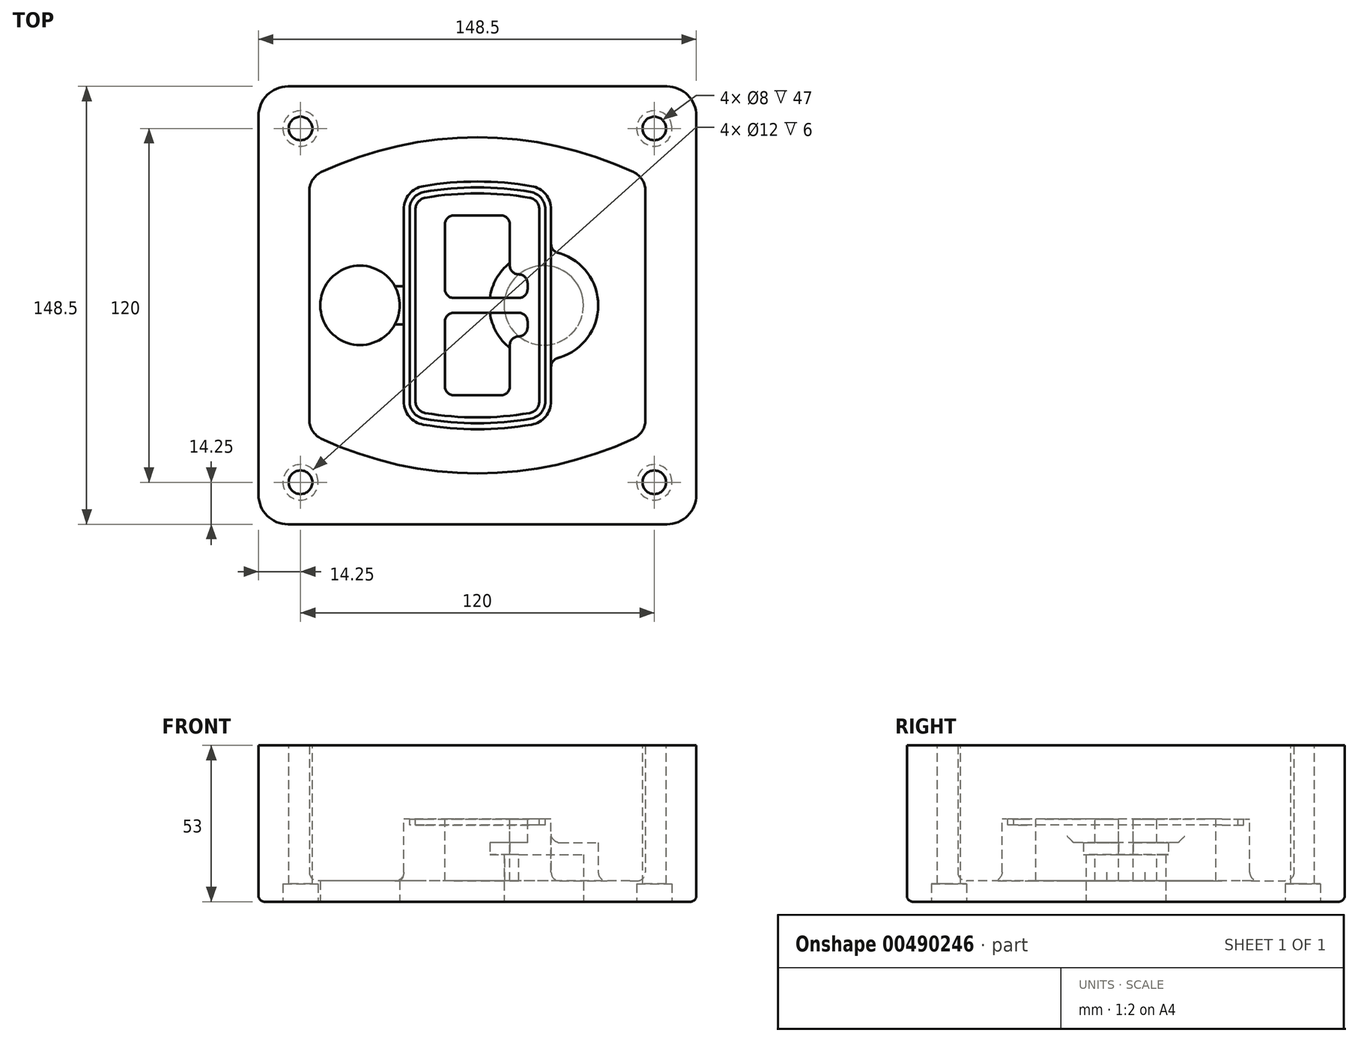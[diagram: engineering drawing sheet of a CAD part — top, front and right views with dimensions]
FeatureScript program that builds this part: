
annotation { "Feature Type Name" : "Feature", "Feature Type Description" : "" }
export const myFeature = defineFeature(function(context is Context, id is Id, definition is map)
    precondition{}
    {
        {
            var Q0;
            Q0=qCreatedBy(makeId("Top.planeOp"),FACE);
            var sketch = newSketch(context, id + "F0", { "sketchPlane" : qUnion([Q0])});
            skPoint(sketch, "E0.rect.middle", {"position": v(0, 0) * mm});
            skLineSegment(sketch, "E1.bottom", {"start": v(-64.25, -74.25) * mm, "end": v(64.25, -74.25) * mm});
            skLineSegment(sketch, "E1.top", {"start": v(-64.25, 74.25) * mm, "end": v(64.25, 74.25) * mm});
            skLineSegment(sketch, "E1.left", {"start": v(-74.25, -64.25) * mm, "end": v(-74.25, 64.25) * mm});
            skLineSegment(sketch, "E1.right", {"start": v(74.25, -64.25) * mm, "end": v(74.25, 64.25) * mm});
            skLineSegment(sketch, "E2", {"start": v(-74.25, 74.25) * mm, "end": v(74.25, -74.25) * mm, "construction": true});
            skLineSegment(sketch, "E3", {"start": v(74.25, 74.25) * mm, "end": v(-74.25, -74.25) * mm, "construction": true});
            skCircle(sketch, "E4", {"center": v(-60, 60) * mm, "radius": 4 * mm});
            skCircle(sketch, "E5", {"center": v(60, 60) * mm, "radius": 4 * mm});
            skCircle(sketch, "E6", {"center": v(60, -60) * mm, "radius": 4 * mm});
            skCircle(sketch, "E7", {"center": v(-60, -60) * mm, "radius": 4 * mm});
            skLineSegment(sketch, "E8", {"start": v(-60, 60) * mm, "end": v(60, 60) * mm, "construction": true});
            skLineSegment(sketch, "E9", {"start": v(60, 60) * mm, "end": v(60, -60) * mm, "construction": true});
            skLineSegment(sketch, "E10", {"start": v(60, -60) * mm, "end": v(-60, -60) * mm, "construction": true});
            skLineSegment(sketch, "E11", {"start": v(-60, -60) * mm, "end": v(-60, 60) * mm, "construction": true});
            skLineSegment(sketch, "E12", {"start": v(-60, 38.83) * mm, "end": v(-60, -38.83) * mm});
            skLineSegment(sketch, "E13", {"start": v(60, 38.83) * mm, "end": v(60, -38.83) * mm});
            skArc(sketch, "E14", {"start": v(54.26, 47.88) * mm, "mid": v(0, 60) * mm, "end": v(-54.26, 47.88) * mm});
            skArc(sketch, "E15", {"start": v(-54.26, -47.88) * mm, "mid": v(0, -60) * mm, "end": v(54.26, -47.88) * mm});
            skLineSegment(sketch, "E16", {"start": v(-60, 0) * mm, "end": v(60, 0) * mm, "construction": true});
            skPoint(sketch, "E17.visualSharp", {"position": v(-60, -45) * mm});
            skArc(sketch, "E17.filletArc", {"start": v(-60, -38.83) * mm, "mid": v(-58.44, -44.2) * mm, "end": v(-54.26, -47.88) * mm});
            skPoint(sketch, "E18.visualSharp", {"position": v(-60, 45) * mm});
            skArc(sketch, "E18.filletArc", {"start": v(-54.26, 47.88) * mm, "mid": v(-58.44, 44.2) * mm, "end": v(-60, 38.83) * mm});
            skPoint(sketch, "E19.visualSharp", {"position": v(60, 45) * mm});
            skArc(sketch, "E19.filletArc", {"start": v(60, 38.83) * mm, "mid": v(58.44, 44.2) * mm, "end": v(54.26, 47.88) * mm});
            skPoint(sketch, "E20.visualSharp", {"position": v(60, -45) * mm});
            skArc(sketch, "E20.filletArc", {"start": v(54.26, -47.88) * mm, "mid": v(58.44, -44.2) * mm, "end": v(60, -38.83) * mm});
            skPoint(sketch, "E21.visualSharp", {"position": v(-74.25, 74.25) * mm});
            skArc(sketch, "E21.filletArc", {"start": v(-64.25, 74.25) * mm, "mid": v(-71.32, 71.32) * mm, "end": v(-74.25, 64.25) * mm});
            skPoint(sketch, "E22.visualSharp", {"position": v(74.25, 74.25) * mm});
            skArc(sketch, "E22.filletArc", {"start": v(74.25, 64.25) * mm, "mid": v(71.32, 71.32) * mm, "end": v(64.25, 74.25) * mm});
            skPoint(sketch, "E23.visualSharp", {"position": v(74.25, -74.25) * mm});
            skArc(sketch, "E23.filletArc", {"start": v(64.25, -74.25) * mm, "mid": v(71.32, -71.32) * mm, "end": v(74.25, -64.25) * mm});
            skPoint(sketch, "E24.visualSharp", {"position": v(-74.25, -74.25) * mm});
            skArc(sketch, "E24.filletArc", {"start": v(-74.25, -64.25) * mm, "mid": v(-71.32, -71.32) * mm, "end": v(-64.25, -74.25) * mm});
            skArc(sketch, "E25.0", {"start": v(57, 38.83) * mm, "mid": v(55.9, 42.58) * mm, "end": v(52.98, 45.17) * mm});
            skLineSegment(sketch, "E25.1", {"start": v(57, 38.83) * mm, "end": v(57, -38.83) * mm});
            skArc(sketch, "E25.2", {"start": v(52.98, -45.17) * mm, "mid": v(55.9, -42.58) * mm, "end": v(57, -38.83) * mm});
            skArc(sketch, "E25.3", {"start": v(-52.98, -45.17) * mm, "mid": v(0, -57) * mm, "end": v(52.98, -45.17) * mm});
            skArc(sketch, "E25.4", {"start": v(-57, -38.83) * mm, "mid": v(-55.9, -42.58) * mm, "end": v(-52.98, -45.17) * mm});
            skArc(sketch, "E25.5", {"start": v(52.98, 45.17) * mm, "mid": v(0, 57) * mm, "end": v(-52.98, 45.17) * mm});
            skLineSegment(sketch, "E25.6", {"start": v(-57, 38.83) * mm, "end": v(-57, -38.83) * mm});
            skArc(sketch, "E25.7", {"start": v(-52.98, 45.17) * mm, "mid": v(-55.9, 42.58) * mm, "end": v(-57, 38.83) * mm});
            skArc(sketch, "E26.0", {"start": v(-55.96, 51.5) * mm, "mid": v(-61.82, 46.33) * mm, "end": v(-64, 38.83) * mm});
            skArc(sketch, "E26.1", {"start": v(55.96, 51.5) * mm, "mid": v(0, 64) * mm, "end": v(-55.96, 51.5) * mm});
            skArc(sketch, "E26.2", {"start": v(64, 38.83) * mm, "mid": v(61.82, 46.33) * mm, "end": v(55.96, 51.5) * mm});
            skLineSegment(sketch, "E26.3", {"start": v(64, 38.83) * mm, "end": v(64, -38.83) * mm});
            skArc(sketch, "E26.4", {"start": v(55.96, -51.5) * mm, "mid": v(61.82, -46.33) * mm, "end": v(64, -38.83) * mm});
            skLineSegment(sketch, "E26.5", {"start": v(-64, 38.83) * mm, "end": v(-64, -38.83) * mm});
            skArc(sketch, "E26.6", {"start": v(-55.96, -51.5) * mm, "mid": v(0, -64) * mm, "end": v(55.96, -51.5) * mm});
            skArc(sketch, "E26.7", {"start": v(-64, -38.83) * mm, "mid": v(-61.82, -46.33) * mm, "end": v(-55.96, -51.5) * mm});
            skSolve(sketch);
        }
        {
            var Q0;
            Q0=makeQuery(id+"F0.imprint","IMPRINT",FACE,{"disambiguationData":[TD([[makeQuery(id+"F0.imprint","IMPRINT",EDGE,{"derivedFrom":sQuery(id+"F0.wireOp",EDGE,"E1.bottom")}),1.0]])]});
            var Q1;
            Q1=makeQuery(id+"F0.imprint","IMPRINT",FACE,{"disambiguationData":[TD([[makeQuery(id+"F0.imprint","IMPRINT",EDGE,{"derivedFrom":sQuery(id+"F0.wireOp",EDGE,"E12")}),1.0]])]});
            var Q2;
            Q2=makeQuery(id+"F0.imprint","IMPRINT",FACE,{"disambiguationData":[TD([[makeQuery(id+"F0.imprint","IMPRINT",EDGE,{"derivedFrom":sQuery(id+"F0.wireOp",EDGE,"E25.0")}),1.0]])]});
            var Q3;
            Q3=makeQuery(id+"F0.imprint","IMPRINT",FACE,{"disambiguationData":[TD([[makeQuery(id+"F0.imprint","IMPRINT",EDGE,{"derivedFrom":sQuery(id+"F0.wireOp",EDGE,"E12")}),-1.0]])]});
            extrude(context, id + "F1", {"entities" : qUnion([Q0, Q1, Q2, Q3]), "oppositeDirection" : true, "depth" : 25 * mm});
        }
        {
            var Q0;
            Q0=makeQuery(id+"F0.imprint","IMPRINT",FACE,{"disambiguationData":[TD([[makeQuery(id+"F0.imprint","IMPRINT",EDGE,{"derivedFrom":sQuery(id+"F0.wireOp",EDGE,"E12")}),1.0]])]});
            extrude(context, id + "F2", {"entities" : qUnion([Q0]), "operationType" : NewBodyOperationType.ADD, "depth" : 3 * mm});
        }
        {
            var Q0;
            Q0=makeQuery(id+"F0.imprint","IMPRINT",FACE,{"disambiguationData":[TD([[makeQuery(id+"F0.imprint","IMPRINT",EDGE,{"derivedFrom":sQuery(id+"F0.wireOp",EDGE,"E25.0")}),1.0]])]});
            extrude(context, id + "F3", {"entities" : qUnion([Q0]), "operationType" : NewBodyOperationType.REMOVE, "oppositeDirection" : true, "depth" : 18 * mm});
        }
        {
            var Q0;
            Q0=makeQuery(id+"F2.opExtrude","CAP_FACE",FACE,{"disambiguationData":[OSD([sQuery(id+"F0.wireOp",EDGE,"E12"),sQuery(id+"F0.wireOp",EDGE,"E13"),sQuery(id+"F0.wireOp",EDGE,"E14"),sQuery(id+"F0.wireOp",EDGE,"E15"),sQuery(id+"F0.wireOp",EDGE,"E17.filletArc"),sQuery(id+"F0.wireOp",EDGE,"E18.filletArc"),sQuery(id+"F0.wireOp",EDGE,"E19.filletArc"),sQuery(id+"F0.wireOp",EDGE,"E20.filletArc"),sQuery(id+"F0.wireOp",EDGE,"E25.0"),sQuery(id+"F0.wireOp",EDGE,"E25.1"),sQuery(id+"F0.wireOp",EDGE,"E25.2"),sQuery(id+"F0.wireOp",EDGE,"E25.3"),sQuery(id+"F0.wireOp",EDGE,"E25.4"),sQuery(id+"F0.wireOp",EDGE,"E25.5"),sQuery(id+"F0.wireOp",EDGE,"E25.6"),sQuery(id+"F0.wireOp",EDGE,"E25.7")])],"isStart":false});
            var sketch = newSketch(context, id + "F4", { "sketchPlane" : qUnion([Q0])});
            skArc(sketch, "E27.0", {"start": v(-18.34, -40.45) * mm, "mid": v(0, -42) * mm, "end": v(18.34, -40.45) * mm});
            skArc(sketch, "E28.0", {"start": v(18.34, 40.45) * mm, "mid": v(0, 42) * mm, "end": v(-18.34, 40.45) * mm});
            skLineSegment(sketch, "E29", {"start": v(-25, 32.57) * mm, "end": v(-25, -32.57) * mm});
            skLineSegment(sketch, "E30", {"start": v(25, 32.57) * mm, "end": v(25, -32.57) * mm});
            skLineSegment(sketch, "E31", {"start": v(-25, 39.1) * mm, "end": v(25, 39.1) * mm, "construction": true});
            skLineSegment(sketch, "E32", {"start": v(-25, -39.1) * mm, "end": v(25, -39.1) * mm, "construction": true});
            skPoint(sketch, "E33.visualSharp", {"position": v(-25, 39.1) * mm});
            skArc(sketch, "E33.filletArc", {"start": v(-18.34, 40.45) * mm, "mid": v(-23.11, 37.73) * mm, "end": v(-25, 32.57) * mm});
            skPoint(sketch, "E34.visualSharp", {"position": v(25, 39.1) * mm});
            skArc(sketch, "E34.filletArc", {"start": v(25, 32.57) * mm, "mid": v(23.11, 37.73) * mm, "end": v(18.34, 40.45) * mm});
            skPoint(sketch, "E35.visualSharp", {"position": v(25, -39.1) * mm});
            skArc(sketch, "E35.filletArc", {"start": v(18.34, -40.45) * mm, "mid": v(23.11, -37.73) * mm, "end": v(25, -32.57) * mm});
            skPoint(sketch, "E36.visualSharp", {"position": v(-25, -39.1) * mm});
            skArc(sketch, "E36.filletArc", {"start": v(-25, -32.57) * mm, "mid": v(-23.11, -37.73) * mm, "end": v(-18.34, -40.45) * mm});
            skArc(sketch, "E37.0", {"start": v(52.98, 45.17) * mm, "mid": v(0, 57) * mm, "end": v(-52.98, 45.17) * mm});
            skArc(sketch, "E37.1", {"start": v(-52.98, 45.17) * mm, "mid": v(-55.9, 42.58) * mm, "end": v(-57, 38.83) * mm});
            skLineSegment(sketch, "E37.2", {"start": v(-57, 38.83) * mm, "end": v(-57, -38.83) * mm});
            skArc(sketch, "E37.3", {"start": v(-57, -38.83) * mm, "mid": v(-55.9, -42.58) * mm, "end": v(-52.98, -45.17) * mm});
            skArc(sketch, "E37.4", {"start": v(-52.98, -45.17) * mm, "mid": v(0, -57) * mm, "end": v(52.98, -45.17) * mm});
            skArc(sketch, "E37.5", {"start": v(52.98, -45.17) * mm, "mid": v(55.9, -42.58) * mm, "end": v(57, -38.83) * mm});
            skLineSegment(sketch, "E37.6", {"start": v(57, 38.83) * mm, "end": v(57, -38.83) * mm});
            skArc(sketch, "E37.7", {"start": v(57, 38.83) * mm, "mid": v(55.9, 42.58) * mm, "end": v(52.98, 45.17) * mm});
            skLineSegment(sketch, "E38.0", {"start": v(23, 32.57) * mm, "end": v(23, -32.57) * mm});
            skArc(sketch, "E38.1", {"start": v(18, -38.48) * mm, "mid": v(21.58, -36.44) * mm, "end": v(23, -32.57) * mm});
            skArc(sketch, "E38.2", {"start": v(-18, -38.48) * mm, "mid": v(0, -40) * mm, "end": v(18, -38.48) * mm});
            skArc(sketch, "E38.3", {"start": v(-23, -32.57) * mm, "mid": v(-21.58, -36.44) * mm, "end": v(-18, -38.48) * mm});
            skLineSegment(sketch, "E38.4", {"start": v(-23, 32.57) * mm, "end": v(-23, -32.57) * mm});
            skArc(sketch, "E38.5", {"start": v(23, 32.57) * mm, "mid": v(21.58, 36.44) * mm, "end": v(18, 38.48) * mm});
            skArc(sketch, "E38.6", {"start": v(-18, 38.48) * mm, "mid": v(-21.58, 36.44) * mm, "end": v(-23, 32.57) * mm});
            skArc(sketch, "E38.7", {"start": v(18, 38.48) * mm, "mid": v(0, 40) * mm, "end": v(-18, 38.48) * mm});
            skArc(sketch, "E39.0", {"start": v(21, 32.57) * mm, "mid": v(20.06, 35.15) * mm, "end": v(17.67, 36.5) * mm});
            skLineSegment(sketch, "E39.1", {"start": v(21, 32.57) * mm, "end": v(21, -32.57) * mm});
            skArc(sketch, "E39.2", {"start": v(17.67, -36.5) * mm, "mid": v(20.06, -35.15) * mm, "end": v(21, -32.57) * mm});
            skArc(sketch, "E39.3", {"start": v(-17.67, -36.5) * mm, "mid": v(0, -38) * mm, "end": v(17.67, -36.5) * mm});
            skArc(sketch, "E39.4", {"start": v(-21, -32.57) * mm, "mid": v(-20.06, -35.15) * mm, "end": v(-17.67, -36.5) * mm});
            skArc(sketch, "E39.5", {"start": v(17.67, 36.5) * mm, "mid": v(0, 38) * mm, "end": v(-17.67, 36.5) * mm});
            skLineSegment(sketch, "E39.6", {"start": v(-21, 32.57) * mm, "end": v(-21, -32.57) * mm});
            skArc(sketch, "E39.7", {"start": v(-17.67, 36.5) * mm, "mid": v(-20.06, 35.15) * mm, "end": v(-21, 32.57) * mm});
            skLineSegment(sketch, "E40", {"start": v(-25, 0) * mm, "end": v(25, 0) * mm, "construction": true});
            skLineSegment(sketch, "E41", {"start": v(-11, 5.5) * mm, "end": v(-11, 27.5) * mm});
            skLineSegment(sketch, "E42", {"start": v(-8, 30.5) * mm, "end": v(8, 30.5) * mm});
            skLineSegment(sketch, "E43", {"start": v(11, 27.5) * mm, "end": v(11, 13.5) * mm});
            skLineSegment(sketch, "E44", {"start": v(14, 10.5) * mm, "end": v(14, 10.5) * mm});
            skLineSegment(sketch, "E45", {"start": v(17, 7.5) * mm, "end": v(17, 5.5) * mm});
            skLineSegment(sketch, "E46", {"start": v(14, 2.5) * mm, "end": v(-8, 2.5) * mm});
            skPoint(sketch, "E47.visualSharp", {"position": v(-11, 30.5) * mm});
            skArc(sketch, "E47.filletArc", {"start": v(-8, 30.5) * mm, "mid": v(-10.12, 29.62) * mm, "end": v(-11, 27.5) * mm});
            skPoint(sketch, "E48.visualSharp", {"position": v(11, 30.5) * mm});
            skArc(sketch, "E48.filletArc", {"start": v(11, 27.5) * mm, "mid": v(10.12, 29.62) * mm, "end": v(8, 30.5) * mm});
            skPoint(sketch, "E49.visualSharp", {"position": v(11, 10.5) * mm});
            skArc(sketch, "E49.filletArc", {"start": v(11, 13.5) * mm, "mid": v(11.88, 11.38) * mm, "end": v(14, 10.5) * mm});
            skPoint(sketch, "E50.visualSharp", {"position": v(17, 10.5) * mm});
            skArc(sketch, "E50.filletArc", {"start": v(17, 7.5) * mm, "mid": v(16.12, 9.62) * mm, "end": v(14, 10.5) * mm});
            skPoint(sketch, "E51.visualSharp", {"position": v(17, 2.5) * mm});
            skArc(sketch, "E51.filletArc", {"start": v(14, 2.5) * mm, "mid": v(16.12, 3.38) * mm, "end": v(17, 5.5) * mm});
            skPoint(sketch, "E52.visualSharp", {"position": v(-11, 2.5) * mm});
            skArc(sketch, "E52.filletArc", {"start": v(-11, 5.5) * mm, "mid": v(-10.12, 3.38) * mm, "end": v(-8, 2.5) * mm});
            skLineSegment(sketch, "E53.0.MirrorCS", {"start": v(14, -2.5) * mm, "end": v(-8, -2.5) * mm});
            skArc(sketch, "E54.0.MirrorCS", {"start": v(-11, -5.5) * mm, "mid": v(-10.12, -3.38) * mm, "end": v(-8, -2.5) * mm});
            skLineSegment(sketch, "E55.0.MirrorCS", {"start": v(-11, -5.5) * mm, "end": v(-11, -27.5) * mm});
            skArc(sketch, "E56.0.MirrorCS", {"start": v(-8, -30.5) * mm, "mid": v(-10.12, -29.62) * mm, "end": v(-11, -27.5) * mm});
            skLineSegment(sketch, "E57.0.MirrorCS", {"start": v(-8, -30.5) * mm, "end": v(8, -30.5) * mm});
            skArc(sketch, "E58.0.MirrorCS", {"start": v(11, -27.5) * mm, "mid": v(10.12, -29.62) * mm, "end": v(8, -30.5) * mm});
            skLineSegment(sketch, "E59.0.MirrorCS", {"start": v(11, -27.5) * mm, "end": v(11, -13.5) * mm});
            skArc(sketch, "E60.0.MirrorCS", {"start": v(11, -13.5) * mm, "mid": v(11.88, -11.38) * mm, "end": v(14, -10.5) * mm});
            skArc(sketch, "E61.0.MirrorCS", {"start": v(17, -7.5) * mm, "mid": v(16.12, -9.62) * mm, "end": v(14, -10.5) * mm});
            skLineSegment(sketch, "E62.0.MirrorCS", {"start": v(17, -7.5) * mm, "end": v(17, -5.5) * mm});
            skArc(sketch, "E63.0.MirrorCS", {"start": v(14, -2.5) * mm, "mid": v(16.12, -3.38) * mm, "end": v(17, -5.5) * mm});
            skSolve(sketch);
        }
        {
            var Q0;
            Q0=makeQuery(id+"F4.imprint","IMPRINT",FACE,{"disambiguationData":[TD([[makeQuery(id+"F4.imprint","IMPRINT",EDGE,{"derivedFrom":sQuery(id+"F4.wireOp",EDGE,"E27.0")}),1.0]])]});
            var Q1;
            Q1=makeQuery(id+"F4.imprint","IMPRINT",FACE,{"disambiguationData":[TD([[makeQuery(id+"F4.imprint","IMPRINT",EDGE,{"derivedFrom":sQuery(id+"F4.wireOp",EDGE,"E38.0")}),-1.0]])]});
            var Q2;
            Q2=makeQuery(id+"F4.imprint","IMPRINT",FACE,{"disambiguationData":[TD([[makeQuery(id+"F4.imprint","IMPRINT",EDGE,{"derivedFrom":sQuery(id+"F4.wireOp",EDGE,"E39.0")}),1.0]])]});
            extrude(context, id + "F5", {"entities" : qUnion([Q0, Q1, Q2]), "operationType" : NewBodyOperationType.ADD, "endBound" : BoundingType.UP_TO_NEXT, "oppositeDirection" : true, "depth" : 25 * mm});
        }
        {
            var Q0;
            Q0=makeQuery(id+"F4.imprint","IMPRINT",FACE,{"disambiguationData":[TD([[makeQuery(id+"F4.imprint","IMPRINT",EDGE,{"derivedFrom":sQuery(id+"F4.wireOp",EDGE,"E38.0")}),-1.0]])]});
            extrude(context, id + "F6", {"entities" : qUnion([Q0]), "operationType" : NewBodyOperationType.REMOVE, "oppositeDirection" : true, "depth" : 2 * mm});
        }
        {
            var Q0;
            Q0=makeQuery(id+"F1.opExtrude","CAP_FACE",FACE,{"disambiguationData":[OSD([sQuery(id+"F0.wireOp",EDGE,"E1.bottom"),sQuery(id+"F0.wireOp",EDGE,"E1.top"),sQuery(id+"F0.wireOp",EDGE,"E1.left"),sQuery(id+"F0.wireOp",EDGE,"E1.right"),sQuery(id+"F0.wireOp",EDGE,"E4"),sQuery(id+"F0.wireOp",EDGE,"E5"),sQuery(id+"F0.wireOp",EDGE,"E6"),sQuery(id+"F0.wireOp",EDGE,"E7"),sQuery(id+"F0.wireOp",EDGE,"E21.filletArc"),sQuery(id+"F0.wireOp",EDGE,"E22.filletArc"),sQuery(id+"F0.wireOp",EDGE,"E23.filletArc"),sQuery(id+"F0.wireOp",EDGE,"E24.filletArc")])],"isStart":false});
            var sketch = newSketch(context, id + "F7", { "sketchPlane" : qUnion([Q0])});
            skCircle(sketch, "E64", {"center": v(22.5, 0) * mm, "radius": 13.47 * mm});
            skCircle(sketch, "E65", {"center": v(-39.81, 0) * mm, "radius": 13.47 * mm});
            skLineSegment(sketch, "E66", {"start": v(74.25, 0) * mm, "end": v(-74.25, 0) * mm});
            skCircle(sketch, "E67", {"center": v(22.5, 0) * mm, "radius": 18.47 * mm});
            skCircle(sketch, "E68", {"center": v(60, -60) * mm, "radius": 6 * mm});
            skCircle(sketch, "E69", {"center": v(-60, -60) * mm, "radius": 6 * mm});
            skCircle(sketch, "E70", {"center": v(-60, 60) * mm, "radius": 6 * mm});
            skCircle(sketch, "E71", {"center": v(60, 60) * mm, "radius": 6 * mm});
            skSolve(sketch);
        }
        {
            var Q0;
            {var subQ1=sQuery(id+"F7.wireOp",EDGE,"E66");var subQ4=sQuery(id+"F7.wireOp",EDGE,"E64");var subQ6=makeQuery(id+"F7.imprint","INTERSECT",VERTEX,{"disambiguationData":[OD(0.0)],"derivedFrom":[subQ4,subQ1]});Q0=makeQuery(id+"F7.imprint","IMPRINT",FACE,{"disambiguationData":[TD([[makeQuery(id+"F7.imprint","IMPRINT",EDGE,{"disambiguationData":[TD([[subQ6,-1.0]])],"derivedFrom":subQ4}),-1.0]])]});}
            var Q1;
            {var subQ0=sQuery(id+"F7.wireOp",EDGE,"E66");var subQ1=sQuery(id+"F7.wireOp",EDGE,"E64");var subQ3=makeQuery(id+"F7.imprint","INTERSECT",VERTEX,{"disambiguationData":[OD(0.0)],"derivedFrom":[subQ1,subQ0]});Q1=makeQuery(id+"F7.imprint","IMPRINT",FACE,{"disambiguationData":[TD([[makeQuery(id+"F7.imprint","IMPRINT",EDGE,{"disambiguationData":[TD([[subQ3,-1.0]])],"derivedFrom":subQ1}),1.0]])]});}
            var Q2;
            {var subQ0=sQuery(id+"F7.wireOp",EDGE,"E66");var subQ1=sQuery(id+"F7.wireOp",EDGE,"E64");var subQ3=makeQuery(id+"F7.imprint","INTERSECT",VERTEX,{"disambiguationData":[OD(0.0)],"derivedFrom":[subQ1,subQ0]});Q2=makeQuery(id+"F7.imprint","IMPRINT",FACE,{"disambiguationData":[TD([[makeQuery(id+"F7.imprint","IMPRINT",EDGE,{"disambiguationData":[TD([[subQ3,1.0]])],"derivedFrom":subQ1}),1.0]])]});}
            var Q3;
            {var subQ1=sQuery(id+"F7.wireOp",EDGE,"E66");var subQ4=sQuery(id+"F7.wireOp",EDGE,"E64");var subQ6=makeQuery(id+"F7.imprint","INTERSECT",VERTEX,{"disambiguationData":[OD(0.0)],"derivedFrom":[subQ4,subQ1]});Q3=makeQuery(id+"F7.imprint","IMPRINT",FACE,{"disambiguationData":[TD([[makeQuery(id+"F7.imprint","IMPRINT",EDGE,{"disambiguationData":[TD([[subQ6,1.0]])],"derivedFrom":subQ4}),-1.0]])]});}
            extrude(context, id + "F8", {"entities" : qUnion([Q0, Q1, Q2, Q3]), "operationType" : NewBodyOperationType.ADD, "oppositeDirection" : true, "depth" : 20 * mm});
        }
        {
            var Q0;
            {var subQ0=sQuery(id+"F7.wireOp",EDGE,"E66");var subQ1=sQuery(id+"F7.wireOp",EDGE,"E64");var subQ3=makeQuery(id+"F7.imprint","INTERSECT",VERTEX,{"disambiguationData":[OD(0.0)],"derivedFrom":[subQ1,subQ0]});Q0=makeQuery(id+"F7.imprint","IMPRINT",FACE,{"disambiguationData":[TD([[makeQuery(id+"F7.imprint","IMPRINT",EDGE,{"disambiguationData":[TD([[subQ3,-1.0]])],"derivedFrom":subQ1}),1.0]])]});}
            var Q1;
            {var subQ0=sQuery(id+"F7.wireOp",EDGE,"E66");var subQ1=sQuery(id+"F7.wireOp",EDGE,"E64");var subQ3=makeQuery(id+"F7.imprint","INTERSECT",VERTEX,{"disambiguationData":[OD(0.0)],"derivedFrom":[subQ1,subQ0]});Q1=makeQuery(id+"F7.imprint","IMPRINT",FACE,{"disambiguationData":[TD([[makeQuery(id+"F7.imprint","IMPRINT",EDGE,{"disambiguationData":[TD([[subQ3,1.0]])],"derivedFrom":subQ1}),1.0]])]});}
            extrude(context, id + "F9", {"entities" : qUnion([Q0, Q1]), "operationType" : NewBodyOperationType.REMOVE, "oppositeDirection" : true, "depth" : 16 * mm});
        }
        {
            var Q0;
            {var subQ0=sQuery(id+"F7.wireOp",EDGE,"E66");var subQ1=sQuery(id+"F7.wireOp",EDGE,"E65");var subQ3=makeQuery(id+"F7.imprint","INTERSECT",VERTEX,{"disambiguationData":[OD(0.0)],"derivedFrom":[subQ1,subQ0]});Q0=makeQuery(id+"F7.imprint","IMPRINT",FACE,{"disambiguationData":[TD([[makeQuery(id+"F7.imprint","IMPRINT",EDGE,{"disambiguationData":[TD([[subQ3,-1.0]])],"derivedFrom":subQ1}),1.0]])]});}
            var Q1;
            {var subQ0=sQuery(id+"F7.wireOp",EDGE,"E66");var subQ1=sQuery(id+"F7.wireOp",EDGE,"E65");var subQ3=makeQuery(id+"F7.imprint","INTERSECT",VERTEX,{"disambiguationData":[OD(0.0)],"derivedFrom":[subQ1,subQ0]});Q1=makeQuery(id+"F7.imprint","IMPRINT",FACE,{"disambiguationData":[TD([[makeQuery(id+"F7.imprint","IMPRINT",EDGE,{"disambiguationData":[TD([[subQ3,1.0]])],"derivedFrom":subQ1}),1.0]])]});}
            extrude(context, id + "F10", {"entities" : qUnion([Q0, Q1]), "operationType" : NewBodyOperationType.REMOVE, "oppositeDirection" : true, "depth" : 25 * mm});
        }
        {
            var Q0;
            Q0=makeQuery(id+"F7.imprint","IMPRINT",FACE,{"disambiguationData":[TD([[makeQuery(id+"F7.imprint","IMPRINT",EDGE,{"derivedFrom":sQuery(id+"F7.wireOp",EDGE,"E68")}),1.0]])]});
            var Q1;
            Q1=makeQuery(id+"F7.imprint","IMPRINT",FACE,{"disambiguationData":[TD([[makeQuery(id+"F7.imprint","IMPRINT",EDGE,{"derivedFrom":makeQuery(id+"F1.opExtrude","CAP_EDGE",EDGE,{"disambiguationData":[OSD([sQuery(id+"F0.wireOp",EDGE,"E5")])],"isStart":false})}),-1.0]])]});
            var Q2;
            Q2=makeQuery(id+"F7.imprint","IMPRINT",FACE,{"disambiguationData":[TD([[makeQuery(id+"F7.imprint","IMPRINT",EDGE,{"derivedFrom":sQuery(id+"F7.wireOp",EDGE,"E69")}),1.0]])]});
            var Q3;
            Q3=makeQuery(id+"F7.imprint","IMPRINT",FACE,{"disambiguationData":[TD([[makeQuery(id+"F7.imprint","IMPRINT",EDGE,{"derivedFrom":makeQuery(id+"F1.opExtrude","CAP_EDGE",EDGE,{"disambiguationData":[OSD([sQuery(id+"F0.wireOp",EDGE,"E4")])],"isStart":false})}),-1.0]])]});
            var Q4;
            Q4=makeQuery(id+"F7.imprint","IMPRINT",FACE,{"disambiguationData":[TD([[makeQuery(id+"F7.imprint","IMPRINT",EDGE,{"derivedFrom":sQuery(id+"F7.wireOp",EDGE,"E70")}),1.0]])]});
            var Q5;
            Q5=makeQuery(id+"F7.imprint","IMPRINT",FACE,{"disambiguationData":[TD([[makeQuery(id+"F7.imprint","IMPRINT",EDGE,{"derivedFrom":makeQuery(id+"F1.opExtrude","CAP_EDGE",EDGE,{"disambiguationData":[OSD([sQuery(id+"F0.wireOp",EDGE,"E7")])],"isStart":false})}),-1.0]])]});
            var Q6;
            Q6=makeQuery(id+"F7.imprint","IMPRINT",FACE,{"disambiguationData":[TD([[makeQuery(id+"F7.imprint","IMPRINT",EDGE,{"derivedFrom":sQuery(id+"F7.wireOp",EDGE,"E71")}),1.0]])]});
            var Q7;
            Q7=makeQuery(id+"F7.imprint","IMPRINT",FACE,{"disambiguationData":[TD([[makeQuery(id+"F7.imprint","IMPRINT",EDGE,{"derivedFrom":makeQuery(id+"F1.opExtrude","CAP_EDGE",EDGE,{"disambiguationData":[OSD([sQuery(id+"F0.wireOp",EDGE,"E6")])],"isStart":false})}),-1.0]])]});
            extrude(context, id + "F11", {"entities" : qUnion([Q0, Q1, Q2, Q3, Q4, Q5, Q6, Q7]), "operationType" : NewBodyOperationType.REMOVE, "oppositeDirection" : true, "depth" : 6 * mm});
        }
        {
            var Q0;
            Q0=makeQuery(id+"F9.boolean.opBoolean","COPY",FACE,{"derivedFrom":makeQuery(id+"F9.opExtrude","CAP_FACE",FACE,{"disambiguationData":[OSD([sQuery(id+"F7.wireOp",EDGE,"E64")])],"isStart":false})});
            var sketch = newSketch(context, id + "F12", { "sketchPlane" : qUnion([Q0])});
            skArc(sketch, "E72.0", {"start": v(11, 14.45) * mm, "mid": v(6.45, 9.13) * mm, "end": v(4.2, 2.5) * mm});
            skArc(sketch, "E72.1", {"start": v(4.2, -2.5) * mm, "mid": v(6.45, -9.13) * mm, "end": v(11, -14.45) * mm});
            skLineSegment(sketch, "E73", {"start": v(4.2, -2.5) * mm, "end": v(14, -2.5) * mm});
            skLineSegment(sketch, "E74.0", {"start": v(14, 2.5) * mm, "end": v(4.2, 2.5) * mm});
            skArc(sketch, "E74.1", {"start": v(14, 2.5) * mm, "mid": v(16.12, 3.38) * mm, "end": v(17, 5.5) * mm});
            skLineSegment(sketch, "E74.2", {"start": v(17, 7.5) * mm, "end": v(17, 5.5) * mm});
            skArc(sketch, "E74.3", {"start": v(17, 7.5) * mm, "mid": v(16.12, 9.62) * mm, "end": v(14, 10.5) * mm});
            skArc(sketch, "E74.4", {"start": v(11, 13.5) * mm, "mid": v(11.88, 11.38) * mm, "end": v(14, 10.5) * mm});
            skLineSegment(sketch, "E74.5", {"start": v(11, 14.45) * mm, "end": v(11, 13.5) * mm});
            skLineSegment(sketch, "E74.7", {"start": v(14, -2.5) * mm, "end": v(4.2, -2.5) * mm});
            skArc(sketch, "E74.8", {"start": v(14, -2.5) * mm, "mid": v(16.12, -3.38) * mm, "end": v(17, -5.5) * mm});
            skLineSegment(sketch, "E74.9", {"start": v(17, -7.5) * mm, "end": v(17, -5.5) * mm});
            skArc(sketch, "E74.10", {"start": v(17, -7.5) * mm, "mid": v(16.12, -9.62) * mm, "end": v(14, -10.5) * mm});
            skArc(sketch, "E74.11", {"start": v(11, -13.5) * mm, "mid": v(11.88, -11.38) * mm, "end": v(14, -10.5) * mm});
            skLineSegment(sketch, "E74.12", {"start": v(11, -14.45) * mm, "end": v(11, -13.5) * mm});
            skPoint(sketch, "E75.orphan", {"position": v(11, -27.5) * mm});
            skPoint(sketch, "E76.orphan", {"position": v(-8, -2.5) * mm});
            skPoint(sketch, "E77.orphan", {"position": v(-8, 2.5) * mm});
            skPoint(sketch, "E78.orphan", {"position": v(11, 27.5) * mm});
            skSolve(sketch);
        }
        {
            var Q0;
            {var subQ7=sQuery(id+"F12.wireOp",EDGE,"E72.0");var subQ14=sQuery(id+"F12.wireOp",EDGE,"E72.1");var subQ16=sQuery(id+"F12.wireOp",EDGE,"E74.1");var subQ18=sQuery(id+"F12.wireOp",EDGE,"E74.8");Q0=qUnion([makeQuery(id+"F12.imprint","IMPRINT",FACE,{"disambiguationData":[TD([[makeQuery(id+"F12.imprint","IMPRINT",EDGE,{"derivedFrom":subQ7}),1.0]])]}),makeQuery(id+"F12.imprint","IMPRINT",FACE,{"disambiguationData":[TD([[makeQuery(id+"F12.imprint","IMPRINT",EDGE,{"derivedFrom":subQ14}),1.0]])]}),makeQuery(id+"F12.imprint","IMPRINT",FACE,{"disambiguationData":[TD([[makeQuery(id+"F12.imprint","IMPRINT",EDGE,{"derivedFrom":subQ16}),1.0]])]}),makeQuery(id+"F12.imprint","IMPRINT",FACE,{"disambiguationData":[TD([[makeQuery(id+"F12.imprint","IMPRINT",EDGE,{"derivedFrom":subQ18}),-1.0]])]})]);}
            var Q1;
            Q1=makeQuery(id+"F5.boolean.opBoolean","SPLIT",FACE,{"disambiguationData":[TD([makeQuery(id+"F5.opExtrude","SWEPT_FACE",FACE,{"disambiguationData":[OSD([sQuery(id+"F4.wireOp",EDGE,"E41")])]})])],"derivedFrom":makeQuery(id+"F3.boolean.opBoolean","COPY",FACE,{"derivedFrom":makeQuery(id+"F3.opExtrude","CAP_FACE",FACE,{"disambiguationData":[OSD([sQuery(id+"F0.wireOp",EDGE,"E25.0"),sQuery(id+"F0.wireOp",EDGE,"E25.1"),sQuery(id+"F0.wireOp",EDGE,"E25.2"),sQuery(id+"F0.wireOp",EDGE,"E25.3"),sQuery(id+"F0.wireOp",EDGE,"E25.4"),sQuery(id+"F0.wireOp",EDGE,"E25.5"),sQuery(id+"F0.wireOp",EDGE,"E25.6"),sQuery(id+"F0.wireOp",EDGE,"E25.7")])],"isStart":false})})});
            extrude(context, id + "F13", {"entities" : qUnion([Q0]), "operationType" : NewBodyOperationType.REMOVE, "endBound" : BoundingType.UP_TO_SURFACE, "endBoundEntityFace" : qUnion([Q1]), "depth" : 25 * mm});
        }
        {
            var Q0;
            Q0=makeQuery(id+"F3.boolean.opBoolean","COPY",EDGE,{"derivedFrom":makeQuery(id+"F3.opExtrude","CAP_EDGE",EDGE,{"disambiguationData":[OSD([sQuery(id+"F0.wireOp",EDGE,"E25.6")])],"isStart":false})});
            var Q1;
            Q1=makeQuery(id+"F8.boolean.opBoolean","INTERSECT",EDGE,{"derivedFrom":[makeQuery(id+"F5.opExtrude","SWEPT_FACE",FACE,{"disambiguationData":[OSD([sQuery(id+"F4.wireOp",EDGE,"E30")])]}),makeQuery(id+"F8.opExtrude","CAP_FACE",FACE,{"disambiguationData":[OSD([sQuery(id+"F7.wireOp",EDGE,"E67")])],"isStart":false})]});
            var Q2;
            Q2=makeQuery(id+"F8.boolean.opBoolean","INTERSECT",EDGE,{"disambiguationData":[OD(1.0)],"derivedFrom":[makeQuery(id+"F5.opExtrude","SWEPT_FACE",FACE,{"disambiguationData":[OSD([sQuery(id+"F4.wireOp",EDGE,"E30")])]}),makeQuery(id+"F8.opExtrude","SWEPT_FACE",FACE,{"disambiguationData":[OSD([sQuery(id+"F7.wireOp",EDGE,"E67")])]})]});
            var Q3;
            {var subQ0=sQuery(id+"F4.wireOp",EDGE,"E30");Q3=makeQuery(id+"F8.boolean.opBoolean","SPLIT",EDGE,{"disambiguationData":[TD([makeQuery(id+"F5.opExtrude","SWEPT_FACE",FACE,{"disambiguationData":[OSD([sQuery(id+"F4.wireOp",EDGE,"E35.filletArc")])]})])],"derivedFrom":makeQuery(id+"F5.opExtrude","CAP_EDGE",EDGE,{"disambiguationData":[OSD([subQ0])],"isStart":false})});}
            var Q4;
            {var subQ0=sQuery(id+"F0.wireOp",EDGE,"E25.7");var subQ1=sQuery(id+"F0.wireOp",EDGE,"E25.1");var subQ2=sQuery(id+"F0.wireOp",EDGE,"E25.6");var subQ3=sQuery(id+"F0.wireOp",EDGE,"E25.5");var subQ4=sQuery(id+"F0.wireOp",EDGE,"E25.4");var subQ5=sQuery(id+"F0.wireOp",EDGE,"E25.0");var subQ6=sQuery(id+"F0.wireOp",EDGE,"E25.2");var subQ7=sQuery(id+"F0.wireOp",EDGE,"E25.3");Q4=makeQuery(id+"F8.boolean.opBoolean","INTERSECT",EDGE,{"derivedFrom":[makeQuery(id+"F5.boolean.opBoolean","SPLIT",FACE,{"disambiguationData":[TD([makeQuery(id+"F2.opExtrude","SWEPT_FACE",FACE,{"disambiguationData":[OSD([subQ5])]})])],"derivedFrom":makeQuery(id+"F3.boolean.opBoolean","COPY",FACE,{"derivedFrom":makeQuery(id+"F3.opExtrude","CAP_FACE",FACE,{"disambiguationData":[OSD([subQ5,subQ1,subQ6,subQ7,subQ4,subQ3,subQ2,subQ0])],"isStart":false})})}),makeQuery(id+"F8.opExtrude","SWEPT_FACE",FACE,{"disambiguationData":[OSD([sQuery(id+"F7.wireOp",EDGE,"E67")])]})]});}
            var Q5;
            Q5=makeQuery(id+"F8.boolean.opBoolean","INTERSECT",EDGE,{"disambiguationData":[OD(0.0)],"derivedFrom":[makeQuery(id+"F5.opExtrude","SWEPT_FACE",FACE,{"disambiguationData":[OSD([sQuery(id+"F4.wireOp",EDGE,"E30")])]}),makeQuery(id+"F8.opExtrude","SWEPT_FACE",FACE,{"disambiguationData":[OSD([sQuery(id+"F7.wireOp",EDGE,"E67")])]})]});
            fillet(context, id + "F14", {"entities" : qUnion([Q0, Q1, Q2, Q3, Q4, Q5]), "radius" : 3 * mm, "tangentPropagation" : true, "allowEdgeOverflow" : false});
        }
        {
            var Q0;
            Q0=makeQuery(id+"F1.opExtrude","CAP_EDGE",EDGE,{"disambiguationData":[OSD([sQuery(id+"F0.wireOp",EDGE,"E1.bottom")])],"isStart":false});
            fillet(context, id + "F15", {"entities" : qUnion([Q0]), "radius" : 2 * mm, "tangentPropagation" : true, "allowEdgeOverflow" : false});
        }
        {
            var Q0;
            {var subQ0=sQuery(id+"F0.wireOp",EDGE,"E21.filletArc");var subQ1=sQuery(id+"F0.wireOp",EDGE,"E7");var subQ2=sQuery(id+"F0.wireOp",EDGE,"E6");var subQ3=sQuery(id+"F0.wireOp",EDGE,"E5");var subQ4=sQuery(id+"F0.wireOp",EDGE,"E4");var subQ5=sQuery(id+"F0.wireOp",EDGE,"E22.filletArc");var subQ6=sQuery(id+"F0.wireOp",EDGE,"E1.bottom");var subQ7=sQuery(id+"F0.wireOp",EDGE,"E1.right");var subQ8=sQuery(id+"F0.wireOp",EDGE,"E1.top");var subQ9=sQuery(id+"F0.wireOp",EDGE,"E1.left");var subQ10=sQuery(id+"F0.wireOp",EDGE,"E23.filletArc");var subQ11=sQuery(id+"F0.wireOp",EDGE,"E24.filletArc");Q0=makeQuery(id+"F2.boolean.opBoolean","SPLIT",FACE,{"disambiguationData":[TD([makeQuery(id+"F1.opExtrude","SWEPT_FACE",FACE,{"disambiguationData":[OSD([subQ6])]})])],"derivedFrom":makeQuery(id+"F1.opExtrude","CAP_FACE",FACE,{"disambiguationData":[OSD([subQ6,subQ8,subQ9,subQ7,subQ4,subQ3,subQ2,subQ1,subQ0,subQ5,subQ10,subQ11])],"isStart":true})});}
            var Q1;
            Q1=makeQuery(id+"F2.opExtrude","CAP_FACE",FACE,{"disambiguationData":[OSD([sQuery(id+"F0.wireOp",EDGE,"E12"),sQuery(id+"F0.wireOp",EDGE,"E13"),sQuery(id+"F0.wireOp",EDGE,"E14"),sQuery(id+"F0.wireOp",EDGE,"E15"),sQuery(id+"F0.wireOp",EDGE,"E17.filletArc"),sQuery(id+"F0.wireOp",EDGE,"E18.filletArc"),sQuery(id+"F0.wireOp",EDGE,"E19.filletArc"),sQuery(id+"F0.wireOp",EDGE,"E20.filletArc"),sQuery(id+"F0.wireOp",EDGE,"E25.0"),sQuery(id+"F0.wireOp",EDGE,"E25.1"),sQuery(id+"F0.wireOp",EDGE,"E25.2"),sQuery(id+"F0.wireOp",EDGE,"E25.3"),sQuery(id+"F0.wireOp",EDGE,"E25.4"),sQuery(id+"F0.wireOp",EDGE,"E25.5"),sQuery(id+"F0.wireOp",EDGE,"E25.6"),sQuery(id+"F0.wireOp",EDGE,"E25.7")])],"isStart":false});
            extrude(context, id + "F16", {"entities" : qUnion([Q0]), "operationType" : NewBodyOperationType.ADD, "endBound" : BoundingType.UP_TO_SURFACE, "endBoundEntityFace" : qUnion([Q1]), "depth" : 25 * mm});
        }
        {
            var Q0;
            Q0=makeQuery(id+"F16.boolean.opBoolean","MERGE",FACE,{"derivedFrom":[makeQuery(id+"F2.opExtrude","CAP_FACE",FACE,{"disambiguationData":[OSD([sQuery(id+"F0.wireOp",EDGE,"E12"),sQuery(id+"F0.wireOp",EDGE,"E13"),sQuery(id+"F0.wireOp",EDGE,"E14"),sQuery(id+"F0.wireOp",EDGE,"E15"),sQuery(id+"F0.wireOp",EDGE,"E17.filletArc"),sQuery(id+"F0.wireOp",EDGE,"E18.filletArc"),sQuery(id+"F0.wireOp",EDGE,"E19.filletArc"),sQuery(id+"F0.wireOp",EDGE,"E20.filletArc"),sQuery(id+"F0.wireOp",EDGE,"E25.0"),sQuery(id+"F0.wireOp",EDGE,"E25.1"),sQuery(id+"F0.wireOp",EDGE,"E25.2"),sQuery(id+"F0.wireOp",EDGE,"E25.3"),sQuery(id+"F0.wireOp",EDGE,"E25.4"),sQuery(id+"F0.wireOp",EDGE,"E25.5"),sQuery(id+"F0.wireOp",EDGE,"E25.6"),sQuery(id+"F0.wireOp",EDGE,"E25.7")])],"isStart":false}),makeQuery(id+"F16.opExtrude","CAP_FACE",FACE,{"disambiguationData":[OSD([sQuery(id+"F0.wireOp",EDGE,"E1.bottom"),sQuery(id+"F0.wireOp",EDGE,"E1.top"),sQuery(id+"F0.wireOp",EDGE,"E1.left"),sQuery(id+"F0.wireOp",EDGE,"E1.right"),sQuery(id+"F0.wireOp",EDGE,"E4"),sQuery(id+"F0.wireOp",EDGE,"E5"),sQuery(id+"F0.wireOp",EDGE,"E6"),sQuery(id+"F0.wireOp",EDGE,"E7"),sQuery(id+"F0.wireOp",EDGE,"E21.filletArc"),sQuery(id+"F0.wireOp",EDGE,"E22.filletArc"),sQuery(id+"F0.wireOp",EDGE,"E23.filletArc"),sQuery(id+"F0.wireOp",EDGE,"E24.filletArc")])],"isStart":false})]});
            extrude(context, id + "F17", {"entities" : qUnion([Q0]), "operationType" : NewBodyOperationType.ADD, "depth" : 25 * mm});
        }
    });
